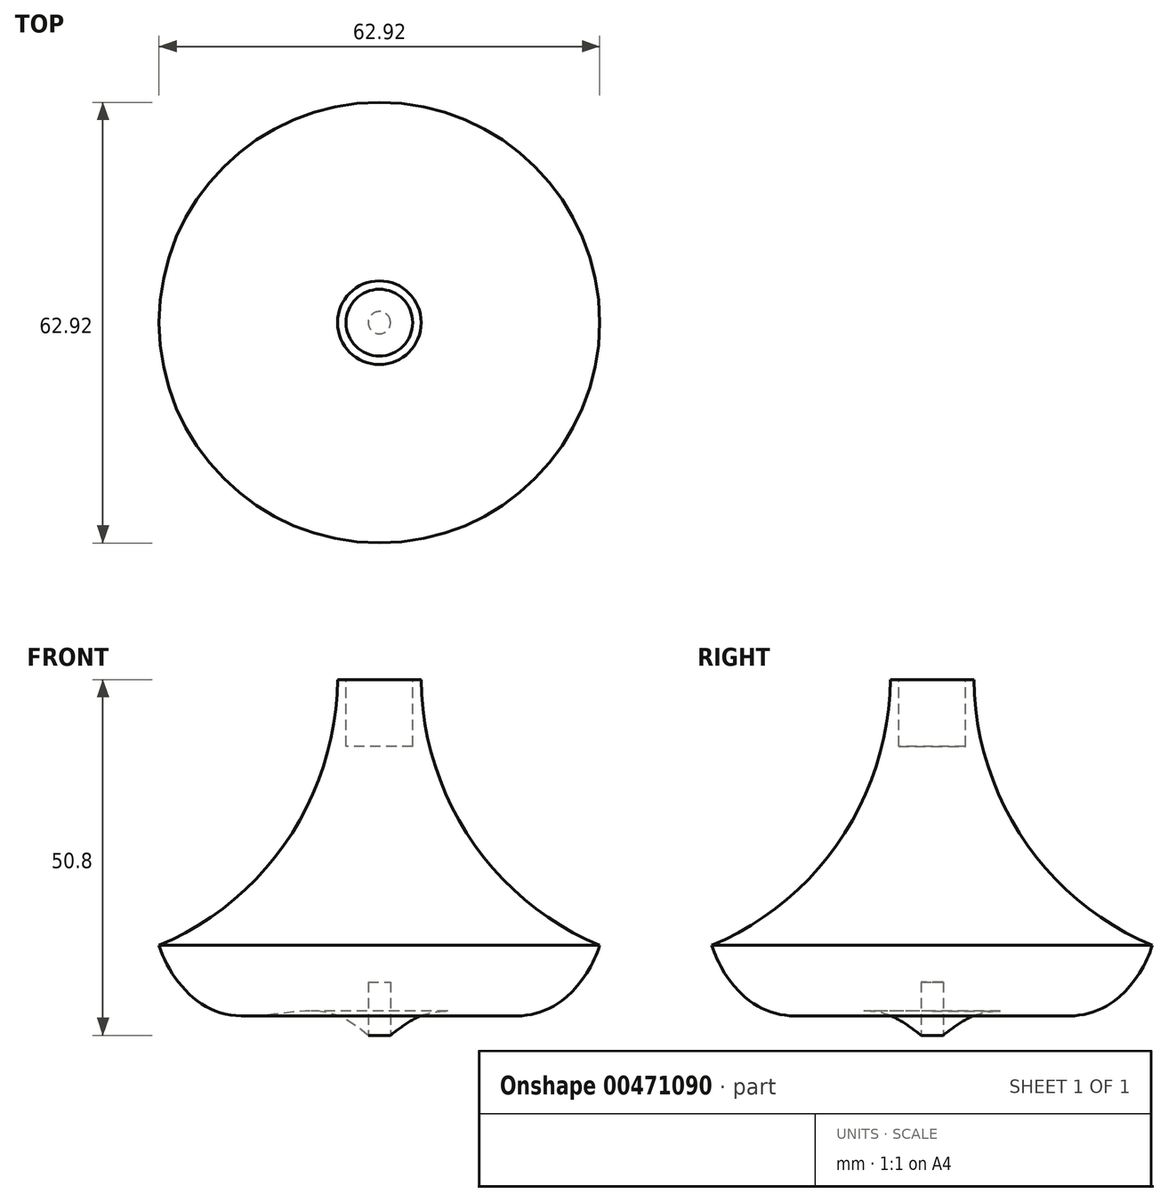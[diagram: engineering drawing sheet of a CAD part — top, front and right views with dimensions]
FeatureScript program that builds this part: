
annotation { "Feature Type Name" : "Feature", "Feature Type Description" : "" }
export const myFeature = defineFeature(function(context is Context, id is Id, definition is map)
    precondition{}
    {
        {
            var Q0;
            Q0=qCreatedBy(makeId("Front.planeOp"),FACE);
            var sketch = newSketch(context, id + "F0", { "sketchPlane" : qUnion([Q0])});
            skLineSegment(sketch, "E0", {"start": v(0, 0) * mm, "end": v(0, 50.8) * mm});
            skLineSegment(sketch, "E1", {"start": v(0, 50.8) * mm, "end": v(5.97, 50.8) * mm});
            skArc(sketch, "E2", {"start": v(5.97, 50.8) * mm, "mid": v(13.03, 28) * mm, "end": v(31.46, 12.84) * mm});
            skLineSegment(sketch, "E3", {"start": v(0, 0) * mm, "end": v(1.59, 0) * mm});
            skFitSpline(sketch, "E4", {"points": [v(1.59, 0) * mm, v(8.37, 3.4) * mm, v(22.6, 3.2) * mm, v(31.46, 12.84) * mm], "startDerivative": vector(20.08, 15.97) * mm, "endDerivative": vector(10.92, 34.55) * mm});
            skSolve(sketch);
        }
        {
            var Q0;
            Q0=makeQuery(id+"F0.imprint","IMPRINT",FACE,{"disambiguationData":[TD([[makeQuery(id+"F0.imprint","IMPRINT",EDGE,{"derivedFrom":sQuery(id+"F0.wireOp",EDGE,"E0")}),-1.0]])]});
            var Q1;
            Q1=sQuery(id+"F0.wireOp",EDGE,"E0");
            revolve(context, id + "F1", {"entities" : qUnion([Q0]), "axis" : qUnion([Q1]), "revolveType" : RevolveType.FULL});
        }
        {
            var Q0;
            Q0=makeQuery(id+"F1.opRevolve","SWEPT_FACE",FACE,{"disambiguationData":[OSD([sQuery(id+"F0.wireOp",EDGE,"E1")])]});
            var sketch = newSketch(context, id + "F2", { "sketchPlane" : qUnion([Q0])});
            skCircle(sketch, "E5", {"center": v(0, 0) * mm, "radius": 4.76 * mm});
            skSolve(sketch);
        }
        {
            var Q0;
            Q0=makeQuery(id+"F2.imprint","IMPRINT",FACE,{"disambiguationData":[TD([[makeQuery(id+"F2.imprint","IMPRINT",EDGE,{"derivedFrom":sQuery(id+"F2.wireOp",EDGE,"E5")}),1.0]])]});
            extrude(context, id + "F3", {"entities" : qUnion([Q0]), "operationType" : NewBodyOperationType.REMOVE, "oppositeDirection" : true, "depth" : 9.52 * mm});
        }
        {
            var Q0;
            Q0=makeQuery(id+"F1.opRevolve","SWEPT_FACE",FACE,{"disambiguationData":[OSD([sQuery(id+"F0.wireOp",EDGE,"E3")])]});
            extrude(context, id + "F4", {"entities" : qUnion([Q0]), "operationType" : NewBodyOperationType.REMOVE, "oppositeDirection" : true, "depth" : 7.62 * mm});
        }
    });
